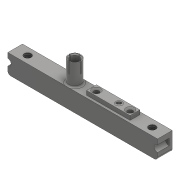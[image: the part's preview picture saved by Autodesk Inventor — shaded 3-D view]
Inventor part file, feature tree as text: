
AUTODESK INVENTOR PART (.ipt)
format: ipt  version: 2018 (Build 220112000, 112)  size: 254,976 bytes
history: native  units: mm
features: sketch x12, extrude x8, hole x3, projected_geometry x3, fillet x2, mirror x1, revolve x1, chamfer x1
ambient origin geometry x8: Origin, YZ Plane, XZ Plane, XY Plane, X Axis, Y Axis, Z Axis, Center Point
bodies: Solid1 (feature_tree)
feature tree (31):
  extrude  "Extrusion1"  Depth=9.0mm
  hole  "Hole1"  [1 undecoded]
  fillet  "Fillet1"  Radius=65.4mm
  hole  "Hole2"  [1 undecoded]
  extrude  "Extrusion2"  Depth=5.8mm
  extrude  "Extrusion3"  Depth=4.5mm
  extrude  "Extrusion4"  Depth=1.6mm
  mirror  "Mirror1"
  fillet  "Fillet2"  Radius=5.0mm
  extrude  "Extrusion5"  Depth=0.8mm
  hole  "Hole3"  [1 undecoded]
  extrude  "Extrusion6"  Depth=36.5mm
  revolve  "Revolution1"  [1 undecoded]
  extrude  "Extrusion7"  Depth=0.508mm
  chamfer  "Chamfer1"  Distance=2.9mm
  extrude  "Extrusion8"  Depth=0.508mm TaperAngle=0.0deg
  sketch  "Sketch1"  dims[d0=71.4mm d1=9.0mm]
  sketch  "Sketch2"  dims[d2=7.0mm d3=0.0mm d4=6.0mm d5=65.4mm]
  sketch  "Sketch3"  dims[d6=3.242mm d7=8.0mm d8=4.0mm d9=2.0mm d10=90.0deg d11=8.0mm d12=0.0mm d13=1.5mm]
  sketch  "Sketch4"  dims[d14=28.4mm]
  sketch  "Sketch5"  dims[d15=4.3mm d16=8.0mm d17=4.0mm d18=2.0mm d19=90.0deg d20=8.0mm d21=0.0mm d22=5.8mm]
  sketch  "Sketch6"  dims[d23=10.2mm d24=0.0mm d25=4.5mm]
  projected_geometry  "Projected Loop1"
  sketch  "Sketch7"  dims[d26=14.3mm d27=0.0mm d28=1.6mm d29=5.0mm]
  sketch  "Sketch8"  dims[d30=5.5mm d31=0.0mm d32=0.8mm]
  projected_geometry  "Projected Loop2"
  sketch  "Sketch9"  dims[d33=1.1mm d34=4.7mm]
  projected_geometry  "Projected Loop3"
  sketch  "Sketch10"  dims[d35=20.7mm d36=36.5mm]
  sketch  "Sketch11"  dims[d37=2.0mm d38=0.0mm d39=38.8mm]
  sketch  "Sketch12"  dims[d40=16.1mm d41=2.4mm d42=8.0mm d43=3.9mm d44=2.0mm d45=90.0deg d46=8.0mm d47=0.0mm d48=2.9mm d49=2.9mm d50=8.0mm d51=0.0mm d52=0.6mm d53=0.6mm d54=10.7mm d55=45.0deg d56=8.0mm d57=0.0mm d58=6.3mm d59=0.2mm d60=10.7mm d61=90.0deg d62=0.5mm d63=1.0mm d64=0.508mm d65=5.1mm d66=0.0mm d67=0.508mm d68=0.4mm d69=2.0mm d70=45.0deg]
note: 4 required parameter values undecoded (feature->parameter linkage not recoverable at this tier; creation-order binding heuristic only, values carry confidence <= 0.55)